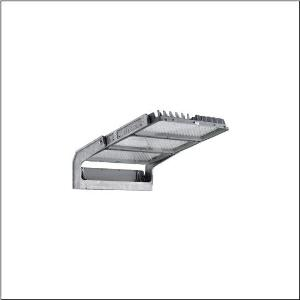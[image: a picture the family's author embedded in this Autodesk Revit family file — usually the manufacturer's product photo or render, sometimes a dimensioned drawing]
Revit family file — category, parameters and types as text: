
# Revit family: floodlight_fl_11_maxi_pro___rs08_5xa779124l02fb_fdbd
name_source: partatom
category: Lighting Fixtures
units: mm (PartAtom-declared; Revit-internal decimal feet)

## family parameters
Cut with Voids When Loaded = No
Host = Face
Light Source = No
Part Type = Normal
Room Calculation Point = No
Round Connector Dimension = Use Diameter
Shared = No

## types (1)
- --- (1 x LED, 129490 lm, 1323.9 W, 5700K)
    Apparent Load = 1324 VA
    CIE Flux Codes = 70 87 98 100 100
    Color Rendering = 90
    Color Temperature = 5700K
    Default Elevation = 1800 mm
    Description = Floodlight FL 11  maxi  pro floodlight; light control with lens of PMMA; cover panel of toughened safety glass, transparent; light distribution: RS08, rotationally symmetric direct distribution, LED; colour temperature: 5700K, rated luminous flux: 129.490lm, colour rendering: CRI > 90, light colour: 957; luminous efficacy: 98lm/W; brightness control: DALI 2; with terminal, 5-pole, max. 2.5mm², mains connection: 220..240V/380..400V AC, 50/60Hz, surge voltage resistance: line to ground: 10kV, LED service life up to 100,000h L90. Typical operating time: 1000h per year., ECG replaceable separately, LED unit replaceable without ESD environment, dustproof LED module, dimming range 10..100%; 1324W floodlight with 3x LED unit of diecast aluminium, coated grey; length: 1.003mm / width: 651mm / height: 338mm; mounting bracket, of diecast aluminium, uncoated, natural, equipment: Power, protection rating (complete): IP66; insulation class (complete): insulation class I (protective earthing); certification: CE, ENEC, VDE; ball protection: ball impact resistant, only for outdoor installations in the designated locations, permissible operating ambient temperature: -45..+55°C, permissible storage temperature: -40..+85°Cpackaging unit: 1 piece

Light Distribution: RS08
    Height = 320 mm
    Lamp = 1 x LED
    Lamp Light Flux = 129490 lm
    Lamp Power = 1323.9 W
    Lamp count = 1
    Length = 1002 mm
    Luminous efficacy = 98 lm/W
    Manufacturer = Siteco
    ModVariant = No
    Model = 5XA779124L02FB
    Mounting Place = Ceiling
    Mounting Type = Surface mounted
    Number of Poles = 1
    OnlyDefault = Yes
    Power Factor = 1
    Product Name = Floodlight FL 11 maxi pro | RS08
    Product group = floodlight | ceiling mounted
    ProductGroupID = 303
    Protection Class = Protection class I
    Protection Degree = IP 66
    RLX_Detail_Level = 1
    RLX_Emergency_Light_Flux = 0 lm
    RLX_Emergency_Type = 0
    RLX_Emergency_Type_DB = No
    RlxData = <blob elided: 40321 chars, md5=1b089ee5>
    Socket = socket
    Standby Power = 0 W
    System Light Flux = 129490 lm
    System Power = 1324 W
    Type Comments = factory setting: luminous flux: 100 % | dim-lin: 254 | 900 mA
    Type Image = l_1356210.jpg
    URL = http://relux.com
    VarID = @adj_040061
    Voltage = 0 V
    Weight = 0.00 kg
    Width = 655 mm

## geometry (parser evidence)
native form markers: Blend x4, Sweep x13
no freeform markers — native parametric forms only
